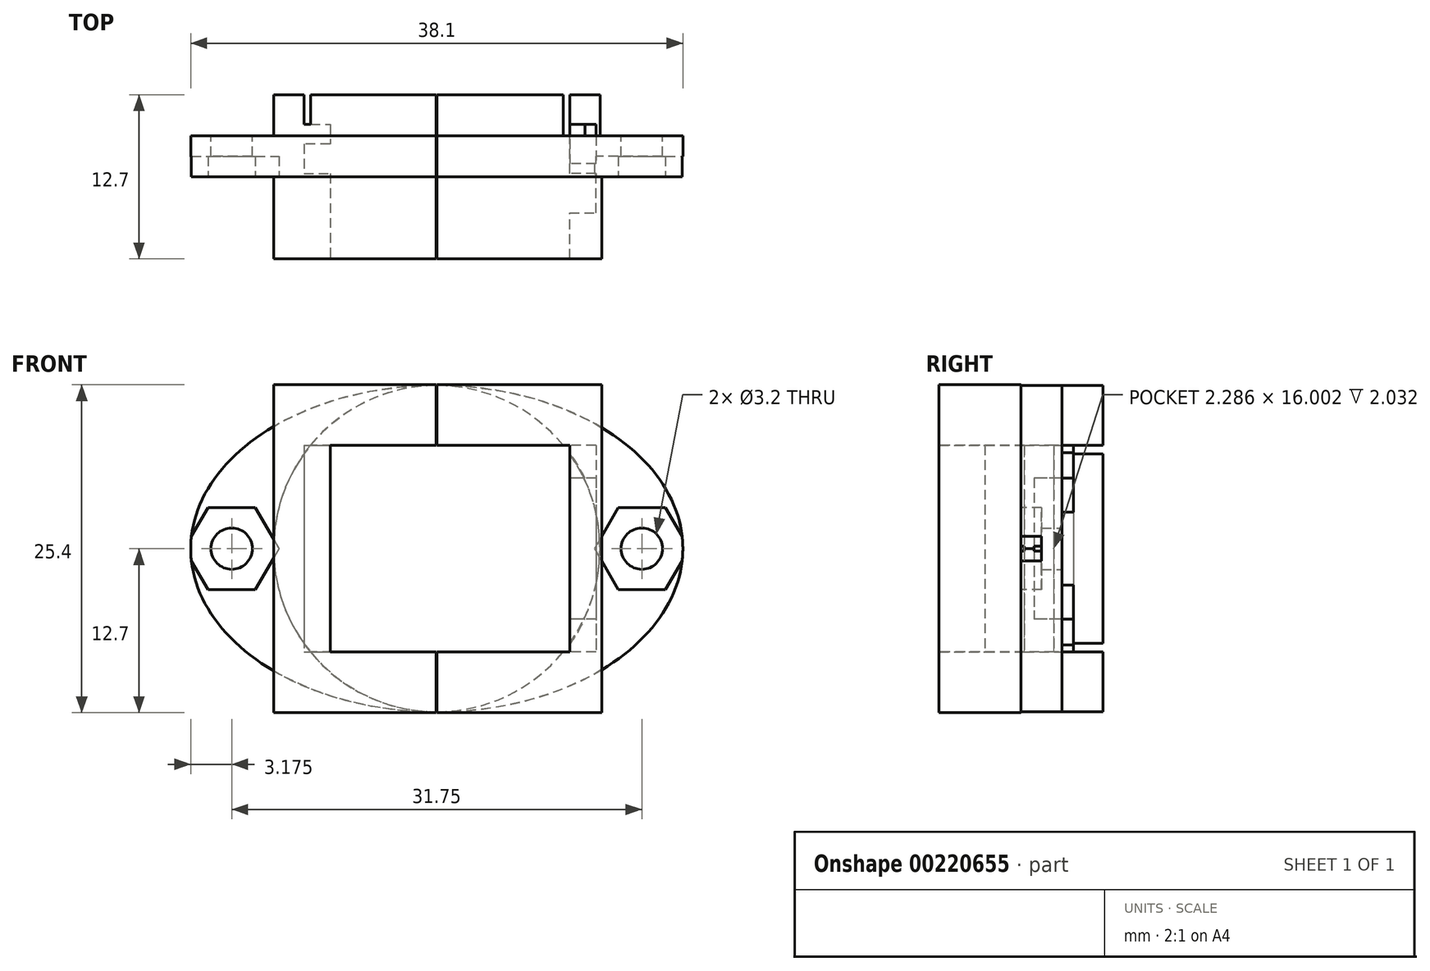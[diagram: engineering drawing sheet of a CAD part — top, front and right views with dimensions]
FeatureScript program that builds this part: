
annotation { "Feature Type Name" : "Feature", "Feature Type Description" : "" }
export const myFeature = defineFeature(function(context is Context, id is Id, definition is map)
    precondition{}
    {
        {
            var Q0;
            Q0=qCreatedBy(makeId("Front.planeOp"),FACE);
            var sketch = newSketch(context, id + "F0", { "sketchPlane" : qUnion([Q0])});
            skCircle(sketch, "E0", {"center": v(0, 0) * mm, "radius": 12.64 * mm});
            skSolve(sketch);
        }
        {
            var Q0;
            Q0 = qSketchRegion(id + "F0", true);
            extrude(context, id + "F1", {"entities" : qUnion([Q0]), "depth" : 12.7 * mm});
        }
        {
            var Q0;
            Q0=qCreatedBy(makeId("Front.planeOp"),FACE);
            var sketch = newSketch(context, id + "F2", { "sketchPlane" : qUnion([Q0])});
            skEllipse(sketch, "E1", {"center": v(0, 0) * mm, "majorRadius": 19.05 * mm, "minorRadius": 12.64 * mm, "majorAxis": v(1, 0)});
            skSolve(sketch);
        }
        {
            var Q0;
            Q0 = qSketchRegion(id + "F2", true);
            extrude(context, id + "F3", {"entities" : qUnion([Q0]), "operationType" : NewBodyOperationType.ADD, "depth" : 6.35 * mm, "hasSecondDirection" : true, "secondDirectionOppositeDirection" : false, "secondDirectionDepth" : 3.17 * mm});
        }
        {
            var Q0;
            Q0=qCreatedBy(makeId("Front.planeOp"),FACE);
            var sketch = newSketch(context, id + "F4", { "sketchPlane" : qUnion([Q0])});
            skCircle(sketch, "E2", {"center": v(15.88, 0) * mm, "radius": 1.6 * mm});
            skCircle(sketch, "E3", {"center": v(-15.88, 0) * mm, "radius": 1.6 * mm});
            skSolve(sketch);
        }
        {
            var Q0;
            Q0 = qSketchRegion(id + "F4", true);
            extrude(context, id + "F5", {"entities" : qUnion([Q0]), "operationType" : NewBodyOperationType.REMOVE, "endBound" : BoundingType.THROUGH_ALL, "depth" : 25.4 * mm});
        }
        {
            var Q0;
            Q0=makeQuery(id+"F3.boolean.opBoolean","SPLIT",FACE,{"disambiguationData":[OD(0.0)],"derivedFrom":makeQuery(id+"F3.opExtrude","CAP_FACE",FACE,{"disambiguationData":[OSD([sQuery(id+"F2.wireOp",EDGE,"E1")])],"isStart":false})});
            var sketch = newSketch(context, id + "F6", { "sketchPlane" : qUnion([Q0])});
            skLineSegment(sketch, "E4", {"start": v(0, 0) * mm, "end": v(0, 5.98) * mm, "construction": true});
            skCircle(sketch, "E5.cCircle", {"center": v(-15.88, 0) * mm, "radius": 3.18 * mm, "construction": true});
            skLineSegment(sketch, "E5.0", {"start": v(-17.7, 3.17) * mm, "end": v(-14.04, 3.17) * mm});
            skLineSegment(sketch, "E5.1", {"start": v(-14.04, 3.18) * mm, "end": v(-12.2, 0) * mm});
            skLineSegment(sketch, "E5.2", {"start": v(-12.2, 0) * mm, "end": v(-14.04, -3.18) * mm});
            skLineSegment(sketch, "E5.3", {"start": v(-14.04, -3.18) * mm, "end": v(-17.7, -3.18) * mm});
            skLineSegment(sketch, "E5.4", {"start": v(-17.7, -3.18) * mm, "end": v(-19.54, 0) * mm});
            skLineSegment(sketch, "E5.5", {"start": v(-19.54, 0) * mm, "end": v(-17.7, 3.17) * mm});
            skPoint(sketch, "E5.0.midPoint", {"position": v(-15.88, 3.17) * mm});
            skLineSegment(sketch, "E6.MirrorCS", {"start": v(17.7, -3.18) * mm, "end": v(19.54, 0) * mm});
            skLineSegment(sketch, "E7.MirrorCS", {"start": v(14.04, -3.18) * mm, "end": v(17.7, -3.18) * mm});
            skLineSegment(sketch, "E8.MirrorCS", {"start": v(12.2, 0) * mm, "end": v(14.04, -3.18) * mm});
            skLineSegment(sketch, "E9.MirrorCS", {"start": v(14.04, 3.18) * mm, "end": v(12.2, 0) * mm});
            skLineSegment(sketch, "E10.MirrorCS", {"start": v(17.7, 3.17) * mm, "end": v(14.04, 3.17) * mm});
            skLineSegment(sketch, "E11.MirrorCS", {"start": v(19.54, 0) * mm, "end": v(17.7, 3.18) * mm});
            skSolve(sketch);
        }
        {
            var Q0;
            Q0 = qSketchRegion(id + "F6", true);
            extrude(context, id + "F7", {"entities" : qUnion([Q0]), "operationType" : NewBodyOperationType.REMOVE, "oppositeDirection" : true, "depth" : 1.59 * mm});
        }
        {
            var Q0;
            Q0=qCreatedBy(makeId("Top.planeOp"),FACE);
            var sketch = newSketch(context, id + "F8", { "sketchPlane" : qUnion([Q0])});
            skLineSegment(sketch, "E12.bottom", {"start": v(12.76, -12.7) * mm, "end": v(-12.64, -12.7) * mm});
            skLineSegment(sketch, "E12.top", {"start": v(12.76, -6.35) * mm, "end": v(-12.64, -6.35) * mm});
            skLineSegment(sketch, "E12.left", {"start": v(12.76, -12.7) * mm, "end": v(12.76, -6.35) * mm});
            skLineSegment(sketch, "E12.right", {"start": v(-12.64, -12.7) * mm, "end": v(-12.64, -6.35) * mm});
            skSolve(sketch);
        }
        {
            var Q0;
            Q0 = qSketchRegion(id + "F8", true);
            extrude(context, id + "F9", {"entities" : qUnion([Q0]), "operationType" : NewBodyOperationType.ADD, "depth" : 12.7 * mm, "hasSecondDirection" : true, "secondDirectionOppositeDirection" : true, "secondDirectionDepth" : 12.7 * mm});
        }
        {
            var Q0;
            Q0=qCreatedBy(makeId("Top.planeOp"),FACE);
            var sketch = newSketch(context, id + "F10", { "sketchPlane" : qUnion([Q0])});
            skLineSegment(sketch, "E13", {"start": v(10.29, 0) * mm, "end": v(-10.29, 0) * mm});
            skLineSegment(sketch, "E14", {"start": v(-10.29, 0) * mm, "end": v(-10.29, -2.29) * mm});
            skLineSegment(sketch, "E15", {"start": v(-10.29, -2.29) * mm, "end": v(-8.26, -2.29) * mm});
            skLineSegment(sketch, "E16", {"start": v(-8.26, -2.29) * mm, "end": v(-8.26, -3.81) * mm});
            skLineSegment(sketch, "E17", {"start": v(-8.26, -3.81) * mm, "end": v(-10.29, -3.81) * mm});
            skLineSegment(sketch, "E18", {"start": v(-10.29, -3.81) * mm, "end": v(-10.29, -6.1) * mm});
            skLineSegment(sketch, "E19", {"start": v(-10.29, -6.1) * mm, "end": v(-8.26, -6.1) * mm});
            skLineSegment(sketch, "E20", {"start": v(-8.26, -6.1) * mm, "end": v(-8.26, -19.15) * mm});
            skLineSegment(sketch, "E21", {"start": v(-8.26, -19.15) * mm, "end": v(10.29, -19.15) * mm});
            skLineSegment(sketch, "E22", {"start": v(10.29, -19.15) * mm, "end": v(10.29, -9.14) * mm});
            skLineSegment(sketch, "E23", {"start": v(10.29, -9.14) * mm, "end": v(12.32, -9.14) * mm});
            skLineSegment(sketch, "E24", {"start": v(12.32, -9.14) * mm, "end": v(12.32, -6.1) * mm});
            skLineSegment(sketch, "E25", {"start": v(12.32, -6.1) * mm, "end": v(10.29, -6.1) * mm});
            skLineSegment(sketch, "E26", {"start": v(10.29, -6.1) * mm, "end": v(10.29, -5.33) * mm});
            skLineSegment(sketch, "E27", {"start": v(10.29, -5.33) * mm, "end": v(12.32, -5.33) * mm});
            skLineSegment(sketch, "E28", {"start": v(12.32, -5.33) * mm, "end": v(12.32, -2.29) * mm});
            skLineSegment(sketch, "E29", {"start": v(12.32, -2.29) * mm, "end": v(10.29, -2.29) * mm});
            skLineSegment(sketch, "E30", {"start": v(10.29, -2.29) * mm, "end": v(10.29, 0) * mm});
            skSolve(sketch);
        }
        {
            var Q0;
            Q0 = qSketchRegion(id + "F10", true);
            extrude(context, id + "F11", {"entities" : qUnion([Q0]), "operationType" : NewBodyOperationType.REMOVE, "depth" : 8 * mm, "hasSecondDirection" : true, "secondDirectionOppositeDirection" : true, "secondDirectionDepth" : 8 * mm});
        }
        {
            var Q0;
            Q0=qCreatedBy(makeId("Front.planeOp"),FACE);
            var sketch = newSketch(context, id + "F12", { "sketchPlane" : qUnion([Q0])});
            skLineSegment(sketch, "E31.bottom", {"start": v(0, 28.28) * mm, "end": v(-0.05, 28.28) * mm});
            skLineSegment(sketch, "E31.top", {"start": v(0, -22.52) * mm, "end": v(-0.05, -22.52) * mm});
            skLineSegment(sketch, "E31.left", {"start": v(0, 28.28) * mm, "end": v(0, -22.52) * mm});
            skLineSegment(sketch, "E31.right", {"start": v(-0.05, 28.28) * mm, "end": v(-0.05, -22.52) * mm});
            skSolve(sketch);
        }
        {
            var Q0;
            Q0 = qSketchRegion(id + "F12", true);
            extrude(context, id + "F13", {"entities" : qUnion([Q0]), "operationType" : NewBodyOperationType.REMOVE, "endBound" : BoundingType.THROUGH_ALL, "depth" : 25.4 * mm});
        }
        {
            var Q0;
            Q0=makeQuery(id+"F11.boolean.opBoolean","COPY",FACE,{"derivedFrom":makeQuery(id+"F11.opExtrude","SWEPT_FACE",FACE,{"disambiguationData":[OSD([sQuery(id+"F10.wireOp",EDGE,"E27")])]})});
            var sketch = newSketch(context, id + "F14", { "sketchPlane" : qUnion([Q0])});
            skLineSegment(sketch, "E32.bottom", {"start": v(-12.32, 8) * mm, "end": v(-10.29, 8) * mm});
            skLineSegment(sketch, "E32.top", {"start": v(-12.32, 5.46) * mm, "end": v(-10.29, 5.46) * mm});
            skLineSegment(sketch, "E32.left", {"start": v(-12.32, 8) * mm, "end": v(-12.32, 5.46) * mm});
            skLineSegment(sketch, "E32.right", {"start": v(-10.29, 8) * mm, "end": v(-10.29, 5.46) * mm});
            skLineSegment(sketch, "E33.bottom", {"start": v(-12.32, -8) * mm, "end": v(-10.29, -8) * mm});
            skLineSegment(sketch, "E33.top", {"start": v(-12.32, -5.46) * mm, "end": v(-10.29, -5.46) * mm});
            skLineSegment(sketch, "E33.left", {"start": v(-12.32, -8) * mm, "end": v(-12.32, -5.46) * mm});
            skLineSegment(sketch, "E33.right", {"start": v(-10.29, -8) * mm, "end": v(-10.29, -5.46) * mm});
            skSolve(sketch);
        }
        {
            var Q0;
            Q0 = qSketchRegion(id + "F14", true);
            extrude(context, id + "F15", {"entities" : qUnion([Q0]), "operationType" : NewBodyOperationType.ADD, "depth" : 3.05 * mm});
        }
        {
            var Q0;
            Q0=makeQuery(id+"F3.boolean.opBoolean","SPLIT",FACE,{"disambiguationData":[OD(1.0)],"derivedFrom":makeQuery(id+"F3.opExtrude","CAP_FACE",FACE,{"disambiguationData":[OSD([sQuery(id+"F2.wireOp",EDGE,"E1")])],"isStart":true})});
            var sketch = newSketch(context, id + "F16", { "sketchPlane" : qUnion([Q0])});
            skCircle(sketch, "E34", {"center": v(0, 0) * mm, "radius": 12.7 * mm});
            skLineSegment(sketch, "E35.bottom", {"start": v(-20.63, -22.05) * mm, "end": v(27, -22.05) * mm});
            skLineSegment(sketch, "E35.top", {"start": v(-20.63, 22) * mm, "end": v(27, 22) * mm});
            skLineSegment(sketch, "E35.left", {"start": v(-20.63, -22.05) * mm, "end": v(-20.63, 22) * mm});
            skLineSegment(sketch, "E35.right", {"start": v(27, -22.05) * mm, "end": v(27, 22) * mm});
            skSolve(sketch);
        }
        {
            var Q0;
            Q0 = qSketchRegion(id + "F16", true);
            extrude(context, id + "F17", {"entities" : qUnion([Q0]), "operationType" : NewBodyOperationType.REMOVE, "depth" : 25.4 * mm});
        }
    });
